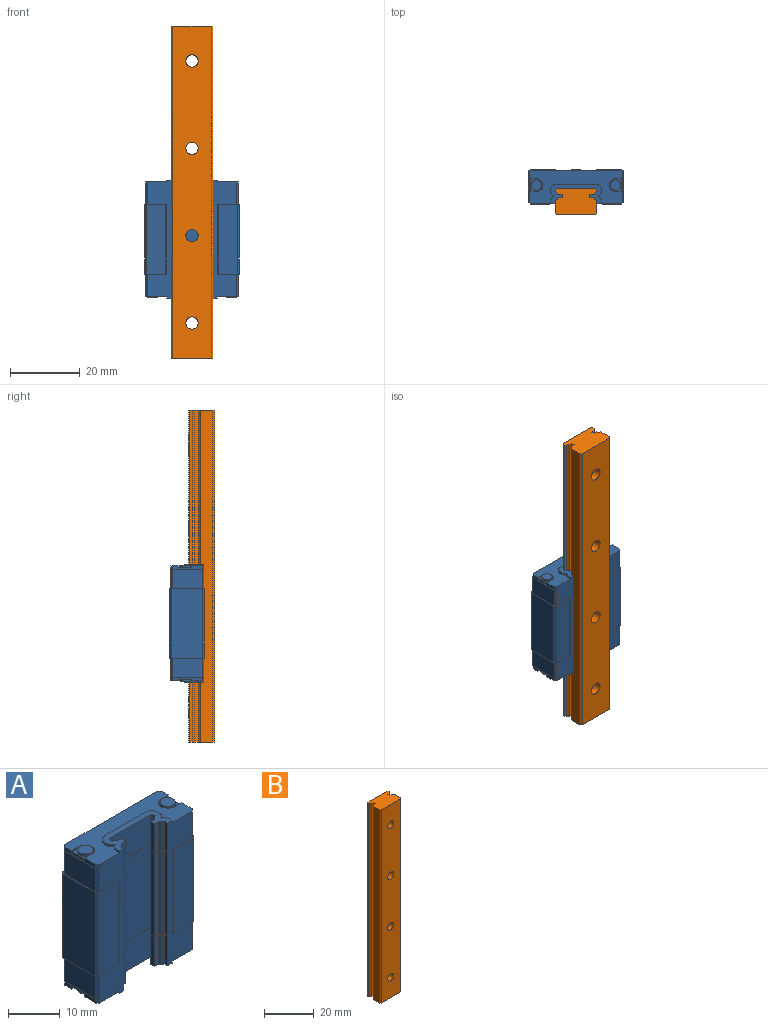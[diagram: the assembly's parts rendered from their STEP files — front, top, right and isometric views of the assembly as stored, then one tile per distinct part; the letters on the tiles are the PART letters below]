
ASSEMBLY  parts=2 mates=1
PART A: 236 faces, bbox 27x10x33.9 mm
  f0: cone r=1.23mm half-angle=60deg, axis (0,1,0), area 5.5mm2, adj f235
  f1: plane 6.95x0.74mm, normal (1,0,0), area 5.1mm2, adj f2,f3,f87,f224
  f2: plane 6.95x0.37mm, normal (0.5,0.87,0), area 3mm2, adj f1,f87,f160,f224
  f3: plane 6.95x0.3mm, normal (0.71,-0.71,0), area 2.9mm2, adj f1,f87,f145,f224
  f4: plane 19.9x0.74mm, normal (1,0,0), area 14.6mm2, adj f141,f142,f200,f223
  f5: plane 6.95x0.74mm, normal (1,0,0), area 5.1mm2, adj f95,f163,f164,f201
  f6: plane 6.95x0.84mm, normal (1,0,0), area 5.8mm2, adj f87,f144,f155,f224
  f7: plane 6.95x0.84mm, normal (-1,0,0), area 5.8mm2, adj f87,f120,f154,f224
  f8: plane 19.9x0.84mm, normal (1,0,0), area 16.6mm2, adj f135,f144,f200,f223
  f9: plane 6.95x0.84mm, normal (1,0,0), area 5.8mm2, adj f95,f144,f168,f201
  f10: plane 6.95x0.84mm, normal (-1,0,0), area 5.8mm2, adj f95,f120,f169,f201
  f11: plane 3x3mm, normal (0,0,-1), area 7.1mm2, adj f12
  f12: cylinder r=1.5mm len=3mm, axis (0,0,1), area 5.7mm2, adj f11,f19
  f13: cylinder r=1.5mm len=3mm, axis (0,0,1), area 5.7mm2, adj f14,f23
  f14: plane 3x3mm, normal (0,0,1), area 7.1mm2, adj f13
  f15: plane 3x3mm, normal (0,0,-1), area 7.1mm2, adj f16
  f16: cylinder r=1.5mm len=3mm, axis (0,0,1), area 5.7mm2, adj f15,f21
  f17: cylinder r=1.5mm len=3mm, axis (0,0,1), area 5.7mm2, adj f18,f25
  f18: plane 3x3mm, normal (0,0,1), area 7.1mm2, adj f17
  f19: plane 3.6x3.55mm, normal (0,0,-1), area 4.3mm2, adj f12,f20,f46,f47,f48
  f20: plane 3.6x0.6mm, normal (1,0,0), area 2.2mm2, adj f19,f41,f46,f48
  f21: plane 3.6x3.55mm, normal (0,0,-1), area 4.3mm2, adj f16,f22,f53,f54,f55
  f22: plane 3.6x0.6mm, normal (-1,0,0), area 2.2mm2, adj f21,f41,f53,f55
  f23: plane 3.6x3.55mm, normal (0,0,1), area 4.3mm2, adj f13,f24,f76,f77,f78
  f24: plane 3.6x0.6mm, normal (1,0,0), area 2.2mm2, adj f23,f71,f76,f78
  f25: plane 3.6x3.55mm, normal (0,0,1), area 4.3mm2, adj f17,f26,f83,f84,f85
  f26: plane 3.6x0.6mm, normal (-1,0,0), area 2.2mm2, adj f25,f71,f83,f85
  f27: plane 26.5x9.5mm, normal (0,0,-1), area 148.2mm2, adj f28,f29,f30,f31,f32,f33,f34,f35
  f28: plane 0.62x0.5mm, normal (-1,0,0), area 0.3mm2, adj f27,f29,f40,f87
  f29: cylinder r=1.6mm len=1.6mm, axis (0,0,1), area 1.3mm2, adj f27,f28,f30,f87
  f30: plane 11.26x0.5mm, normal (0,1,0), area 5.6mm2, adj f27,f29,f31,f87
  f31: cylinder r=1.6mm len=1.6mm, axis (0,0,1), area 1.3mm2, adj f27,f30,f32,f87
  f32: plane 0.62x0.5mm, normal (1,0,0), area 0.3mm2, adj f27,f31,f33,f87
  f33: cylinder r=1.3mm len=1.21mm, axis (0,0,1), area 0.8mm2, adj f27,f32,f34,f87
  f34: cylinder r=0.1mm len=0.5mm, axis (0,0,1), area 0.1mm2, adj f27,f33,f35,f87
  f35: cylinder r=1.3mm len=1.21mm, axis (0,0,1), area 0.8mm2, adj f27,f34,f36,f87
  f36: plane 0.79x0.5mm, normal (1,0,0), area 0.4mm2, adj f27,f35,f87,f120
  f37: plane 0.79x0.5mm, normal (-1,0,0), area 0.4mm2, adj f27,f38,f87,f144
  f38: cylinder r=1.3mm len=1.21mm, axis (0,0,1), area 0.8mm2, adj f27,f37,f39,f87
  f39: cylinder r=0.1mm len=0.5mm, axis (0,0,1), area 0.1mm2, adj f27,f38,f40,f87
  f40: cylinder r=1.3mm len=1.21mm, axis (0,0,1), area 0.8mm2, adj f27,f28,f39,f87
  f41: plane 26.6x9.6mm, normal (0,0,-1), area 5.1mm2, adj f20,f22,f42,f43,f44,f45,f46,f48
  f42: plane 1x0.5mm, normal (-0.71,0.71,0), area 0.7mm2, adj f27,f41,f43,f56
  f43: plane 25.5x1mm, normal (0,1,0), area 25.5mm2, adj f27,f41,f42,f44
  f44: plane 1x0.5mm, normal (0.71,0.71,0), area 0.7mm2, adj f27,f41,f43,f45
  f45: plane 1.9x1mm, normal (1,0,0), area 1.9mm2, adj f27,f41,f44,f46
  f46: plane 1.95x1mm, normal (0,-1,0), area 0.9mm2, adj f19,f20,f27,f41,f45,f47
  f47: cylinder r=1.8mm len=3.6mm, axis (0,0,1), area 2.3mm2, adj f19,f27,f46,f48
  f48: plane 1.95x1mm, normal (0,1,0), area 0.9mm2, adj f19,f20,f27,f41,f47,f49
  f49: plane 3x1mm, normal (1,0,0), area 3mm2, adj f27,f41,f48,f50
  f50: plane 1x0.5mm, normal (0.71,-0.71,0), area 0.7mm2, adj f27,f41,f49,f120
  f51: plane 1x0.5mm, normal (-0.71,-0.71,0), area 0.7mm2, adj f27,f41,f52,f144
  f52: plane 3x1mm, normal (-1,0,0), area 3mm2, adj f27,f41,f51,f53
  f53: plane 1.95x1mm, normal (0,1,0), area 0.9mm2, adj f21,f22,f27,f41,f52,f54
  f54: cylinder r=1.8mm len=3.6mm, axis (0,0,1), area 2.3mm2, adj f21,f27,f53,f55
  f55: plane 1.95x1mm, normal (0,-1,0), area 0.9mm2, adj f21,f22,f27,f41,f54,f56
  f56: plane 1.9x1mm, normal (-1,0,0), area 1.9mm2, adj f27,f41,f42,f55
  f57: plane 26.5x9.5mm, normal (0,0,1), area 148.2mm2, adj f58,f59,f60,f61,f62,f63,f64,f65
  f58: plane 0.62x0.5mm, normal (-1,0,0), area 0.3mm2, adj f57,f59,f70,f95
  f59: cylinder r=1.6mm len=1.6mm, axis (0,0,-1), area 1.3mm2, adj f57,f58,f60,f95
  f60: plane 11.26x0.5mm, normal (0,1,0), area 5.6mm2, adj f57,f59,f61,f95
  f61: cylinder r=1.6mm len=1.6mm, axis (0,0,-1), area 1.3mm2, adj f57,f60,f62,f95
  f62: plane 0.62x0.5mm, normal (1,0,0), area 0.3mm2, adj f57,f61,f63,f95
  f63: cylinder r=1.3mm len=1.21mm, axis (0,0,-1), area 0.8mm2, adj f57,f62,f64,f95
  f64: cylinder r=0.1mm len=0.5mm, axis (0,0,-1), area 0.1mm2, adj f57,f63,f65,f95
  f65: cylinder r=1.3mm len=1.21mm, axis (0,0,-1), area 0.8mm2, adj f57,f64,f66,f95
  f66: plane 0.79x0.5mm, normal (1,0,0), area 0.4mm2, adj f57,f65,f95,f120
  f67: plane 0.79x0.5mm, normal (-1,0,0), area 0.4mm2, adj f57,f68,f95,f144
  f68: cylinder r=1.3mm len=1.21mm, axis (0,0,-1), area 0.8mm2, adj f57,f67,f69,f95
  f69: cylinder r=0.1mm len=0.5mm, axis (0,0,-1), area 0.1mm2, adj f57,f68,f70,f95
  f70: cylinder r=1.3mm len=1.21mm, axis (0,0,-1), area 0.8mm2, adj f57,f58,f69,f95
  f71: plane 26.6x9.6mm, normal (0,0,1), area 5.1mm2, adj f24,f26,f72,f73,f74,f75,f76,f78
  f72: plane 1x0.5mm, normal (-0.71,0.71,0), area 0.7mm2, adj f57,f71,f73,f86
  f73: plane 25.5x1mm, normal (0,1,0), area 25.5mm2, adj f57,f71,f72,f74
  f74: plane 1x0.5mm, normal (0.71,0.71,0), area 0.7mm2, adj f57,f71,f73,f75
  f75: plane 1.9x1mm, normal (1,0,0), area 1.9mm2, adj f57,f71,f74,f76
  f76: plane 1.95x1mm, normal (0,-1,0), area 0.9mm2, adj f23,f24,f57,f71,f75,f77
  f77: cylinder r=1.8mm len=3.6mm, axis (0,0,-1), area 2.3mm2, adj f23,f57,f76,f78
  f78: plane 1.95x1mm, normal (0,1,0), area 0.9mm2, adj f23,f24,f57,f71,f77,f79
  f79: plane 3x1mm, normal (1,0,0), area 3mm2, adj f57,f71,f78,f80
  f80: plane 1x0.5mm, normal (0.71,-0.71,0), area 0.7mm2, adj f57,f71,f79,f120
  f81: plane 1x0.5mm, normal (-0.71,-0.71,0), area 0.7mm2, adj f57,f71,f82,f144
  f82: plane 3x1mm, normal (-1,0,0), area 3mm2, adj f57,f71,f81,f83
  f83: plane 1.95x1mm, normal (0,1,0), area 0.9mm2, adj f25,f26,f57,f71,f82,f84
  f84: cylinder r=1.8mm len=3.6mm, axis (0,0,-1), area 2.3mm2, adj f25,f57,f83,f85
  f85: plane 1.95x1mm, normal (0,-1,0), area 0.9mm2, adj f25,f26,f57,f71,f84,f86
  f86: plane 1.9x1mm, normal (-1,0,0), area 1.9mm2, adj f57,f71,f72,f85
  f87: plane 14.46x5.63mm, normal (0,0,-1), area 31.8mm2, adj f1,f2,f3,f6,f7,f28,f29,f30
  f88: plane 25.6x5.5mm, normal (0,1,0), area 140.8mm2, adj f41,f89,f94,f104
  f89: plane 5.5x0.5mm, normal (0.71,0.71,0), area 3.9mm2, adj f41,f88,f90,f104
  f90: plane 8.6x5.5mm, normal (1,0,0), area 47.3mm2, adj f41,f89,f91,f104
  f91: plane 5.5x0.5mm, normal (0.71,-0.71,0), area 3.9mm2, adj f41,f90,f104,f120
  f92: plane 5.5x0.5mm, normal (-0.71,-0.71,0), area 3.9mm2, adj f41,f93,f104,f144
  f93: plane 8.6x5.5mm, normal (-1,0,0), area 47.3mm2, adj f41,f92,f94,f104
  f94: plane 5.5x0.5mm, normal (-0.71,0.71,0), area 3.9mm2, adj f41,f88,f93,f104
  f95: plane 14.46x5.63mm, normal (0,0,1), area 31.8mm2, adj f5,f9,f10,f58,f59,f60,f61,f62
  f96: plane 25.6x5.5mm, normal (0,1,0), area 140.8mm2, adj f71,f97,f102,f103
  f97: plane 5.5x0.5mm, normal (0.71,0.71,0), area 3.9mm2, adj f71,f96,f98,f103
  f98: plane 8.6x5.5mm, normal (1,0,0), area 47.3mm2, adj f71,f97,f99,f103
  f99: plane 5.5x0.5mm, normal (0.71,-0.71,0), area 3.9mm2, adj f71,f98,f103,f120
  f100: plane 5.5x0.5mm, normal (-0.71,-0.71,0), area 3.9mm2, adj f71,f101,f103,f144
  f101: plane 8.6x5.5mm, normal (-1,0,0), area 47.3mm2, adj f71,f100,f102,f103
  f102: plane 5.5x0.5mm, normal (-0.71,0.71,0), area 3.9mm2, adj f71,f96,f101,f103
  f103: plane 27x10mm, normal (0,0,1), area 11.1mm2, adj f96,f97,f98,f99,f100,f101,f102,f105
  f104: plane 27x10mm, normal (0,0,-1), area 11.1mm2, adj f88,f89,f90,f91,f92,f93,f94,f105
  f105: plane 19.9x0.5mm, normal (-0.71,0.71,0), area 14.1mm2, adj f103,f104,f106,f124
  f106: plane 19.9x7.2mm, normal (0,1,0), area 129.1mm2, adj f103,f104,f105,f107,f225,f231
  f107: plane 19.9x0.4mm, normal (0.53,0.85,0), area 9.4mm2, adj f103,f104,f106,f108
  f108: plane 19.9x3.8mm, normal (0,1,0), area 75.6mm2, adj f103,f104,f107,f109
  f109: plane 19.9x0.4mm, normal (-0.53,0.85,0), area 9.4mm2, adj f103,f104,f108,f110
  f110: plane 19.9x2.4mm, normal (0,1,0), area 47.8mm2, adj f103,f104,f109,f111
  f111: plane 19.9x0.4mm, normal (0.53,0.85,0), area 9.4mm2, adj f103,f104,f110,f112
  f112: plane 19.9x3.8mm, normal (0,1,0), area 75.6mm2, adj f103,f104,f111,f113
  f113: plane 19.9x0.4mm, normal (-0.53,0.85,0), area 9.4mm2, adj f103,f104,f112,f114
  f114: plane 19.9x7.2mm, normal (0,1,0), area 129.1mm2, adj f103,f104,f113,f115,f228,f234
  f115: plane 19.9x0.5mm, normal (0.71,0.71,0), area 14.1mm2, adj f103,f104,f114,f116
  f116: plane 19.9x9mm, normal (1,0,0), area 179.1mm2, adj f103,f104,f115,f117
  f117: plane 19.9x0.5mm, normal (0.71,-0.71,0), area 14.1mm2, adj f103,f104,f116,f118
  f118: plane 19.9x5.5mm, normal (0,-1,0), area 109.5mm2, adj f103,f104,f117,f119
  f119: plane 19.9x0.22mm, normal (-0.41,-0.91,0), area 4.9mm2, adj f103,f104,f118,f120
  f120: plane 33.9x6.8mm, normal (0,-1,0), area 114.9mm2, adj f7,f10,f27,f36,f41,f50,f57,f66
  f121: plane 19.9x0.22mm, normal (0.41,-0.91,0), area 4.9mm2, adj f103,f104,f122,f144
  f122: plane 19.9x5.5mm, normal (0,-1,0), area 109.5mm2, adj f103,f104,f121,f123
  f123: plane 19.9x0.5mm, normal (-0.71,-0.71,0), area 14.1mm2, adj f103,f104,f122,f124
  f124: plane 19.9x9mm, normal (-1,0,0), area 179.1mm2, adj f103,f104,f105,f123
  f125: plane 19.9x11.4mm, normal (0,-1,0), area 226.9mm2, adj f126,f142,f200,f223
  f126: plane 19.9x0.3mm, normal (-0.71,-0.71,0), area 8.4mm2, adj f125,f127,f200,f223
  f127: plane 19.9x0.74mm, normal (-1,0,0), area 14.6mm2, adj f126,f128,f200,f223
  f128: plane 19.9x0.37mm, normal (-0.5,0.87,0), area 8.5mm2, adj f127,f129,f200,f223
  f129: cylinder r=1.32mm len=19.9mm, axis (0,0,1), area 15.3mm2, adj f128,f130,f200,f223
  f130: plane 19.9x1.11mm, normal (0,1,0), area 22.1mm2, adj f129,f131,f200,f223
  f131: plane 19.9x1mm, normal (-1,0,0), area 19.9mm2, adj f130,f132,f200,f223
  f132: plane 19.9x1.11mm, normal (0,-1,0), area 22.1mm2, adj f131,f133,f200,f223
  f133: cylinder r=1.32mm len=19.9mm, axis (0,0,1), area 15.3mm2, adj f132,f134,f200,f223
  f134: plane 19.9x0.37mm, normal (-0.5,-0.87,0), area 8.5mm2, adj f133,f143,f200,f223
  f135: plane 19.9x0.37mm, normal (0.5,-0.87,0), area 8.5mm2, adj f8,f136,f200,f223
  f136: cylinder r=1.32mm len=19.9mm, axis (0,0,1), area 15.3mm2, adj f135,f137,f200,f223
  f137: plane 19.9x1.11mm, normal (0,-1,0), area 22.1mm2, adj f136,f138,f200,f223
  f138: plane 19.9x1mm, normal (1,0,0), area 19.9mm2, adj f137,f139,f200,f223
  f139: plane 19.9x1.11mm, normal (0,1,0), area 22.1mm2, adj f138,f140,f200,f223
  f140: cylinder r=1.32mm len=19.9mm, axis (0,0,1), area 15.3mm2, adj f139,f141,f200,f223
  f141: plane 19.9x0.37mm, normal (0.5,0.87,0), area 8.5mm2, adj f4,f140,f200,f223
  f142: plane 19.9x0.3mm, normal (0.71,-0.71,0), area 8.4mm2, adj f4,f125,f200,f223
  f143: plane 19.9x0.84mm, normal (-1,0,0), area 16.6mm2, adj f120,f134,f200,f223
  f144: plane 33.9x6.8mm, normal (0,-1,0), area 114.9mm2, adj f6,f8,f9,f27,f37,f41,f51,f57
  f145: plane 11.4x6.95mm, normal (0,-1,0), area 79.2mm2, adj f3,f87,f146,f224
  f146: plane 6.95x0.3mm, normal (-0.71,-0.71,0), area 2.9mm2, adj f87,f145,f147,f224
  f147: plane 6.95x0.74mm, normal (-1,0,0), area 5.1mm2, adj f87,f146,f148,f224
  f148: plane 6.95x0.37mm, normal (-0.5,0.87,0), area 3mm2, adj f87,f147,f149,f224
  f149: cylinder r=1.32mm len=6.95mm, axis (0,0,1), area 5.3mm2, adj f87,f148,f150,f224
  f150: plane 6.95x1.11mm, normal (0,1,0), area 7.7mm2, adj f87,f149,f151,f224
  f151: plane 6.95x1mm, normal (-1,0,0), area 6.9mm2, adj f87,f150,f152,f224
  f152: plane 6.95x1.11mm, normal (0,-1,0), area 7.7mm2, adj f87,f151,f153,f224
  f153: cylinder r=1.32mm len=6.95mm, axis (0,0,1), area 5.3mm2, adj f87,f152,f154,f224
  f154: plane 6.95x0.37mm, normal (-0.5,-0.87,0), area 3mm2, adj f7,f87,f153,f224
  f155: plane 6.95x0.37mm, normal (0.5,-0.87,0), area 3mm2, adj f6,f87,f156,f224
  f156: cylinder r=1.32mm len=6.95mm, axis (0,0,1), area 5.3mm2, adj f87,f155,f157,f224
  f157: plane 6.95x1.11mm, normal (0,-1,0), area 7.7mm2, adj f87,f156,f158,f224
  f158: plane 6.95x1mm, normal (1,0,0), area 6.9mm2, adj f87,f157,f159,f224
  f159: plane 6.95x1.11mm, normal (0,1,0), area 7.7mm2, adj f87,f158,f160,f224
  f160: cylinder r=1.32mm len=6.95mm, axis (0,0,1), area 5.3mm2, adj f2,f87,f159,f224
  f161: cylinder r=1.32mm len=6.95mm, axis (0,0,1), area 5.3mm2, adj f95,f162,f163,f201
  f162: plane 6.95x1.11mm, normal (0,1,0), area 7.7mm2, adj f95,f161,f165,f201
  f163: plane 6.95x0.37mm, normal (0.5,0.87,0), area 3mm2, adj f5,f95,f161,f201
  f164: plane 6.95x0.3mm, normal (0.71,-0.71,0), area 2.9mm2, adj f5,f95,f178,f201
  f165: plane 6.95x1mm, normal (1,0,0), area 6.9mm2, adj f95,f162,f166,f201
  f166: plane 6.95x1.11mm, normal (0,-1,0), area 7.7mm2, adj f95,f165,f167,f201
  f167: cylinder r=1.32mm len=6.95mm, axis (0,0,1), area 5.3mm2, adj f95,f166,f168,f201
  f168: plane 6.95x0.37mm, normal (0.5,-0.87,0), area 3mm2, adj f9,f95,f167,f201
  f169: plane 6.95x0.37mm, normal (-0.5,-0.87,0), area 3mm2, adj f10,f95,f170,f201
  f170: cylinder r=1.32mm len=6.95mm, axis (0,0,1), area 5.3mm2, adj f95,f169,f171,f201
  f171: plane 6.95x1.11mm, normal (0,-1,0), area 7.7mm2, adj f95,f170,f172,f201
  f172: plane 6.95x1mm, normal (-1,0,0), area 6.9mm2, adj f95,f171,f173,f201
  f173: plane 6.95x1.11mm, normal (0,1,0), area 7.7mm2, adj f95,f172,f174,f201
  f174: cylinder r=1.32mm len=6.95mm, axis (0,0,1), area 5.3mm2, adj f95,f173,f175,f201
  f175: plane 6.95x0.37mm, normal (-0.5,0.87,0), area 3mm2, adj f95,f174,f176,f201
  f176: plane 6.95x0.74mm, normal (-1,0,0), area 5.1mm2, adj f95,f175,f177,f201
  f177: plane 6.95x0.3mm, normal (-0.71,-0.71,0), area 2.9mm2, adj f95,f176,f178,f201
  f178: plane 11.4x6.95mm, normal (0,-1,0), area 79.2mm2, adj f95,f164,f177,f201
  f179: plane 0.89x0.05mm, normal (1,0,0), area 0mm2, adj f144,f180,f200,f201
  f180: plane 0.34x0.18mm, normal (0.46,-0.89,0), area 0mm2, adj f179,f181,f200,f201
  f181: cylinder r=1.27mm len=0.59mm, axis (0,0,1), area 0mm2, adj f180,f182,f200,f201
  f182: plane 1.09x0.05mm, normal (0,-1,0), area 0.1mm2, adj f181,f183,f200,f201
  f183: plane 0.9x0.05mm, normal (1,0,0), area 0mm2, adj f182,f184,f200,f201
  f184: plane 1.09x0.05mm, normal (0,1,0), area 0.1mm2, adj f183,f185,f200,f201
  f185: cylinder r=1.27mm len=0.59mm, axis (0,0,1), area 0mm2, adj f184,f186,f200,f201
  f186: plane 0.34x0.18mm, normal (0.46,0.89,0), area 0mm2, adj f185,f187,f200,f201
  f187: plane 0.84x0.05mm, normal (1,0,0), area 0mm2, adj f186,f188,f200,f201
  f188: plane 0.3x0.3mm, normal (0.71,-0.71,0), area 0mm2, adj f187,f189,f200,f201
  f189: plane 11.5x0.05mm, normal (0,-1,0), area 0.6mm2, adj f188,f190,f200,f201
  f190: plane 0.3x0.3mm, normal (-0.71,-0.71,0), area 0mm2, adj f189,f191,f200,f201
  f191: plane 0.84x0.05mm, normal (-1,0,0), area 0mm2, adj f190,f192,f200,f201
  f192: plane 0.34x0.18mm, normal (-0.46,0.89,0), area 0mm2, adj f191,f193,f200,f201
  f193: cylinder r=1.27mm len=0.59mm, axis (0,0,1), area 0mm2, adj f192,f194,f200,f201
  f194: plane 1.09x0.05mm, normal (0,1,0), area 0.1mm2, adj f193,f195,f200,f201
  f195: plane 0.9x0.05mm, normal (-1,0,0), area 0mm2, adj f194,f196,f200,f201
  f196: plane 1.09x0.05mm, normal (0,-1,0), area 0.1mm2, adj f195,f197,f200,f201
  f197: cylinder r=1.27mm len=0.59mm, axis (0,0,1), area 0mm2, adj f196,f198,f200,f201
  f198: plane 0.34x0.18mm, normal (-0.46,-0.89,0), area 0mm2, adj f197,f199,f200,f201
  f199: plane 0.89x0.05mm, normal (-1,0,0), area 0mm2, adj f120,f198,f200,f201
  f200: plane 12.1x4.45mm, normal (0,0,1), area 1.4mm2, adj f4,f8,f120,f125,f126,f127,f128,f129
  f201: plane 12.1x4.45mm, normal (0,0,-1), area 1.4mm2, adj f5,f9,f10,f120,f144,f161,f162,f163
  f202: plane 0.89x0.05mm, normal (1,0,0), area 0mm2, adj f144,f203,f223,f224
  f203: plane 0.34x0.18mm, normal (0.46,-0.89,0), area 0mm2, adj f202,f204,f223,f224
  f204: cylinder r=1.27mm len=0.59mm, axis (0,0,-1), area 0mm2, adj f203,f205,f223,f224
  f205: plane 1.09x0.05mm, normal (0,-1,0), area 0.1mm2, adj f204,f206,f223,f224
  f206: plane 0.9x0.05mm, normal (1,0,0), area 0mm2, adj f205,f207,f223,f224
  f207: plane 1.09x0.05mm, normal (0,1,0), area 0.1mm2, adj f206,f208,f223,f224
  f208: cylinder r=1.27mm len=0.59mm, axis (0,0,-1), area 0mm2, adj f207,f209,f223,f224
  f209: plane 0.34x0.18mm, normal (0.46,0.89,0), area 0mm2, adj f208,f210,f223,f224
  f210: plane 0.84x0.05mm, normal (1,0,0), area 0mm2, adj f209,f211,f223,f224
  f211: plane 0.3x0.3mm, normal (0.71,-0.71,0), area 0mm2, adj f210,f212,f223,f224
  f212: plane 11.5x0.05mm, normal (0,-1,0), area 0.6mm2, adj f211,f213,f223,f224
  f213: plane 0.3x0.3mm, normal (-0.71,-0.71,0), area 0mm2, adj f212,f214,f223,f224
  f214: plane 0.84x0.05mm, normal (-1,0,0), area 0mm2, adj f213,f215,f223,f224
  f215: plane 0.34x0.18mm, normal (-0.46,0.89,0), area 0mm2, adj f214,f216,f223,f224
  f216: cylinder r=1.27mm len=0.59mm, axis (0,0,-1), area 0mm2, adj f215,f217,f223,f224
  f217: plane 1.09x0.05mm, normal (0,1,0), area 0.1mm2, adj f216,f218,f223,f224
  f218: plane 0.9x0.05mm, normal (-1,0,0), area 0mm2, adj f217,f219,f223,f224
  f219: plane 1.09x0.05mm, normal (0,-1,0), area 0.1mm2, adj f218,f220,f223,f224
  f220: cylinder r=1.27mm len=0.59mm, axis (0,0,-1), area 0mm2, adj f219,f221,f223,f224
  f221: plane 0.34x0.18mm, normal (-0.46,-0.89,0), area 0mm2, adj f220,f222,f223,f224
  f222: plane 0.89x0.05mm, normal (-1,0,0), area 0mm2, adj f120,f221,f223,f224
  f223: plane 12.1x4.45mm, normal (0,0,-1), area 1.4mm2, adj f4,f8,f120,f125,f126,f127,f128,f129
  f224: plane 12.1x4.45mm, normal (0,0,1), area 1.4mm2, adj f1,f2,f3,f6,f7,f120,f144,f145
  f225: cone r=1.5mm half-angle=45deg, axis (0,1,0), area 3.3mm2, adj f106,f226
  f226: cylinder r=1.23mm len=6.23mm, axis (0,1,0), area 48.1mm2, adj f225,f227
  f227: cone r=1.23mm half-angle=60deg, axis (0,1,0), area 5.5mm2, adj f226
  f228: cone r=1.5mm half-angle=45deg, axis (0,1,0), area 3.3mm2, adj f114,f229
  f229: cylinder r=1.23mm len=6.23mm, axis (0,1,0), area 48.1mm2, adj f228,f230
  f230: cone r=1.23mm half-angle=60deg, axis (0,1,0), area 5.5mm2, adj f229
  f231: cone r=1.5mm half-angle=45deg, axis (0,1,0), area 3.3mm2, adj f106,f232
  f232: cylinder r=1.23mm len=6.23mm, axis (0,1,0), area 48.1mm2, adj f231,f233
  f233: cone r=1.23mm half-angle=60deg, axis (0,1,0), area 5.5mm2, adj f232
  f234: cone r=1.5mm half-angle=45deg, axis (0,1,0), area 3.3mm2, adj f114,f235
  f235: cylinder r=1.23mm len=6.23mm, axis (0,1,0), area 48.1mm2, adj f0,f234
PART B: 38 faces, bbox 12x7.5x95 mm
  f0: plane 95x0.37mm, normal (0.5,-0.87,0), area 40.4mm2, adj f1,f2,f6,f8
  f1: plane 95x0.74mm, normal (1,0,0), area 69.8mm2, adj f0,f6,f7,f8
  f2: cylinder r=1.32mm len=95mm, axis (0,0,1), area 73.1mm2, adj f0,f6,f8,f37
  f3: plane 95x0.3mm, normal (-0.71,0.71,0), area 40.3mm2, adj f4,f5,f6,f8
  f4: plane 95x0.74mm, normal (-1,0,0), area 69.8mm2, adj f3,f6,f8,f25
  f5: plane 95x11.4mm, normal (0,1,0), area 969.9mm2, adj f3,f6,f7,f8,f9,f12,f15,f18
  f6: plane 12x7.5mm, normal (0,0,1), area 84mm2, adj f0,f1,f2,f3,f4,f5,f7,f21
  f7: plane 95x0.3mm, normal (0.71,0.71,0), area 40.3mm2, adj f1,f5,f6,f8
  f8: plane 12x7.5mm, normal (0,0,-1), area 84mm2, adj f0,f1,f2,f3,f4,f5,f7,f21
  f9: cylinder r=3mm len=6mm, axis (0,1,0), area 84.8mm2, adj f5,f10
  f10: plane 6x6mm, normal (0,1,0), area 18.7mm2, adj f9,f11
  f11: cylinder r=1.75mm len=3.5mm, axis (0,1,0), area 33mm2, adj f10,f21
  f12: cylinder r=3mm len=6mm, axis (0,1,0), area 84.8mm2, adj f5,f13
  f13: plane 6x6mm, normal (0,1,0), area 18.7mm2, adj f12,f14
  f14: cylinder r=1.75mm len=3.5mm, axis (0,1,0), area 33mm2, adj f13,f21
  f15: cylinder r=3mm len=6mm, axis (0,1,0), area 84.8mm2, adj f5,f16
  f16: plane 6x6mm, normal (0,1,0), area 18.7mm2, adj f15,f17
  f17: cylinder r=1.75mm len=3.5mm, axis (0,1,0), area 33mm2, adj f16,f21
  f18: cylinder r=3mm len=6mm, axis (0,1,0), area 84.8mm2, adj f5,f19
  f19: plane 6x6mm, normal (0,1,0), area 18.7mm2, adj f18,f20
  f20: cylinder r=1.75mm len=3.5mm, axis (0,1,0), area 33mm2, adj f19,f21
  f21: plane 95x11mm, normal (0,-1,0), area 1006.5mm2, adj f6,f8,f11,f14,f17,f20,f30,f31
  f22: plane 95x1.11mm, normal (0,-1,0), area 105.6mm2, adj f6,f8,f23,f24
  f23: plane 95x1mm, normal (-1,0,0), area 95mm2, adj f6,f8,f22,f26
  f24: cylinder r=1.32mm len=95mm, axis (0,0,1), area 73.1mm2, adj f6,f8,f22,f25
  f25: plane 95x0.37mm, normal (-0.5,-0.87,0), area 40.4mm2, adj f4,f6,f8,f24
  f26: plane 95x1.11mm, normal (0,1,0), area 105.6mm2, adj f6,f8,f23,f27
  f27: cylinder r=1.32mm len=95mm, axis (0,0,1), area 73.1mm2, adj f6,f8,f26,f28
  f28: plane 95x0.37mm, normal (-0.5,0.87,0), area 40.4mm2, adj f6,f8,f27,f29
  f29: plane 95x3.44mm, normal (-1,0,0), area 326.3mm2, adj f6,f8,f28,f30
  f30: plane 95x0.5mm, normal (-0.71,-0.71,0), area 67.2mm2, adj f6,f8,f21,f29
  f31: plane 95x0.5mm, normal (0.71,-0.71,0), area 67.2mm2, adj f6,f8,f21,f32
  f32: plane 95x3.44mm, normal (1,0,0), area 326.3mm2, adj f6,f8,f31,f33
  f33: plane 95x0.37mm, normal (0.5,0.87,0), area 40.4mm2, adj f6,f8,f32,f34
  f34: cylinder r=1.32mm len=95mm, axis (0,0,1), area 73.1mm2, adj f6,f8,f33,f35
  f35: plane 95x1.11mm, normal (0,1,0), area 105.6mm2, adj f6,f8,f34,f36
  f36: plane 95x1mm, normal (1,0,0), area 95mm2, adj f6,f8,f35,f37
  f37: plane 95x1.11mm, normal (0,-1,0), area 105.6mm2, adj f2,f6,f8,f36
PLACE A at identity
PLACE B t=(0,0,13.55)mm
MATE slider B.f8 <-> A.f87  axis (0,0,-1) through (4,5.2,-33.95)mm
